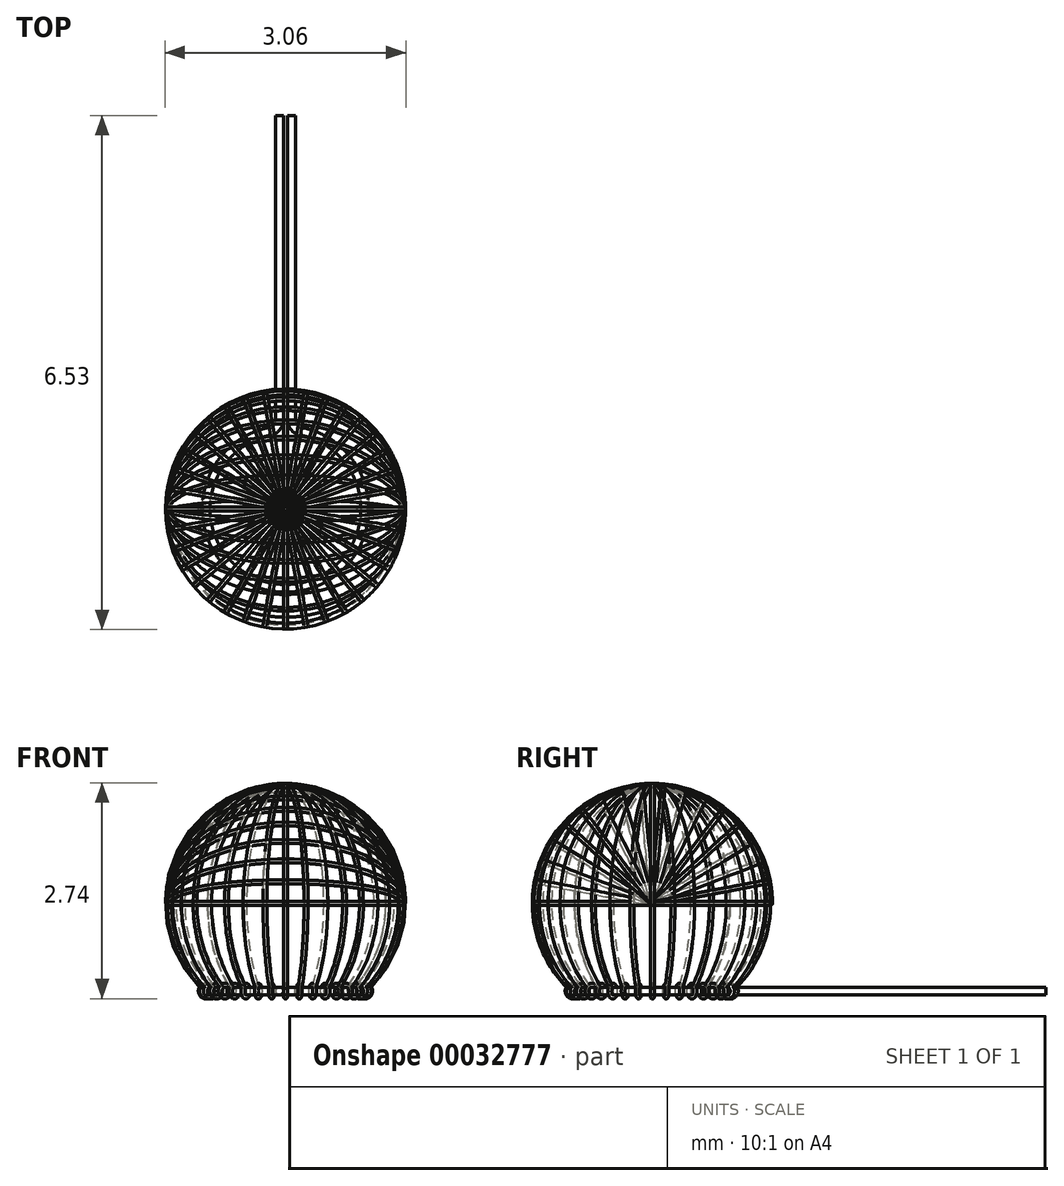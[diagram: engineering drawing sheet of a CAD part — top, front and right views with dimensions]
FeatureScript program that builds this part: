
annotation { "Feature Type Name" : "Feature", "Feature Type Description" : "" }
export const myFeature = defineFeature(function(context is Context, id is Id, definition is map)
    precondition{}
    {
        {
            var Q0;
            Q0=qCreatedBy(makeId("Right.planeOp"),FACE);
            var sketch = newSketch(context, id + "F0", { "sketchPlane" : qUnion([Q0])});
            skArc(sketch, "E0", {"start": v(1.06, -1.06) * mm, "mid": v(0, 1.5) * mm, "end": v(-1.06, -1.06) * mm});
            skSolve(sketch);
        }
        {
            var Q0;
            Q0=qCreatedBy(makeId("Right.planeOp"),FACE);
            var sketch = newSketch(context, id + "F1", { "sketchPlane" : qUnion([Q0])});
            skLineSegment(sketch, "E1", {"start": v(0, 2.55) * mm, "end": v(0, -1.6) * mm});
            skSolve(sketch);
        }
        {
            var Q0;
            Q0=qCreatedBy(makeId("Top.planeOp"),FACE);
            var sketch = newSketch(context, id + "F2", { "sketchPlane" : qUnion([Q0])});
            skArc(sketch, "E2", {"start": v(-1.5, 0) * mm, "mid": v(0, -1.5) * mm, "end": v(1.5, 0) * mm});
            skSolve(sketch);
        }
        {
            var Q0;
            Q0=qCreatedBy(makeId("Front.planeOp"),FACE);
            var sketch = newSketch(context, id + "F3", { "sketchPlane" : qUnion([Q0])});
            skCircle(sketch, "E3", {"center": v(1.5, 0) * mm, "radius": 0.03 * mm});
            skSolve(sketch);
        }
        {
            var Q0;
            Q0 = qSketchRegion(id + "F3", true);
            var Q1;
            Q1=sQuery(id+"F2.wireOp",EDGE,"E2");
            sweep(context, id + "F4", {"profiles" : qUnion([Q0]), "path" : qUnion([Q1])});
        }
        {
            var Q0;
            Q0=qCreatedBy(makeId("Top.planeOp"),FACE);
            var sketch = newSketch(context, id + "F5", { "sketchPlane" : qUnion([Q0])});
            skLineSegment(sketch, "E4", {"start": v(-2.16, 0) * mm, "end": v(2.32, 0) * mm});
            skSolve(sketch);
        }
        {
            var Q0;
            Q0=makeQuery(id+"F4.opSweep","SWEPT_BODY",BODY,{"disambiguationData":[OSD([sQuery(id+"F2.wireOp",EDGE,"E2"),sQuery(id+"F3.wireOp",EDGE,"E3")])]});
            var Q1;
            Q1=sQuery(id+"F5.wireOp",EDGE,"E4");
            circularPattern(context, id + "F6", {"entities" : qUnion([Q0]), "axis" : qUnion([Q1]), "angle" : 180 * degree, "instanceCount" : 18, "oppositeDirection" : true, "equalSpace" : true});
        }
        {
            var Q0;
            Q0=qCreatedBy(makeId("Right.planeOp"),FACE);
            cPlane(context, id + "F7", {"entities" : qUnion([Q0]), "cplaneType" : CPlaneType.OFFSET, "offset" : .5 * mm, "width" : 150 * mm, "height" : 150 * mm});
        }
        {
            var Q0;
            Q0=qCreatedBy(id+"F7.planeOp",FACE);
            var sketch = newSketch(context, id + "F8", { "sketchPlane" : qUnion([Q0])});
            skLineSegment(sketch, "E5", {"start": v(0, 0) * mm, "end": v(-1.06, -1.06) * mm});
            skSolve(sketch);
        }
        {
            var Q0;
            Q0=sQuery(id+"F8.wireOp",EDGE,"E5");
            cPlane(context, id + "F9", {"entities" : qUnion([Q0]), "cplaneType" : CPlaneType.LINE_ANGLE, "offset" : 0 * mm, "angle" : 0 * degree, "width" : 150 * mm, "height" : 150 * mm});
        }
        {
            var Q0;
            Q0=qCreatedBy(id+"F9.planeOp",FACE);
            var sketch = newSketch(context, id + "F10", { "sketchPlane" : qUnion([Q0])});
            skCircle(sketch, "E6", {"center": v(0, -1.5) * mm, "radius": 0.03 * mm});
            skSolve(sketch);
        }
        {
            var Q0;
            Q0=makeQuery(id+"F10.imprint","IMPRINT",FACE,{"disambiguationData":[TD([[makeQuery(id+"F10.imprint","IMPRINT",EDGE,{"derivedFrom":sQuery(id+"F10.wireOp",EDGE,"E6")}),1.0]])]});
            var Q1;
            Q1=sQuery(id+"F0.wireOp",EDGE,"E0");
            sweep(context, id + "F11", {"profiles" : qUnion([Q0]), "path" : qUnion([Q1])});
        }
        {
            var Q0;
            Q0=makeQuery(id+"F11.opSweep","SWEPT_BODY",BODY,{"disambiguationData":[OSD([sQuery(id+"F0.wireOp",EDGE,"E0"),sQuery(id+"F10.wireOp",EDGE,"E6")])]});
            var Q1;
            Q1=sQuery(id+"F1.wireOp",EDGE,"E1");
            circularPattern(context, id + "F12", {"entities" : qUnion([Q0]), "axis" : qUnion([Q1]), "angle" : 360 * degree, "instanceCount" : 36, "equalSpace" : true});
        }
        {
            var Q0;
            Q0=qCreatedBy(makeId("Right.planeOp"),FACE);
            var sketch = newSketch(context, id + "F13", { "sketchPlane" : qUnion([Q0])});
            skLineSegment(sketch, "E7", {"start": v(0, 0) * mm, "end": v(-1.06, -1.06) * mm});
            skCircle(sketch, "E8", {"center": v(-1, -1.11) * mm, "radius": 0.07 * mm});
            skCircle(sketch, "E9", {"center": v(1, -1.11) * mm, "radius": 0.02 * mm});
            skSolve(sketch);
        }
        {
            var Q0;
            Q0=sQuery(id+"F13.wireOp",VERTEX,"E7.end");
            var Q1;
            Q1=sQuery(id+"F13.wireOp",EDGE,"E8");
            cPlane(context, id + "F14", {"entities" : qUnion([Q0, Q1]), "cplaneType" : CPlaneType.CURVE_POINT, "offset" : 150 * mm, "width" : 150 * mm, "height" : 150 * mm});
        }
        {
            var Q0;
            Q0=qCreatedBy(id+"F14.planeOp",FACE);
            var sketch = newSketch(context, id + "F15", { "sketchPlane" : qUnion([Q0])});
            skCircle(sketch, "E10", {"center": v(0, 0) * mm, "radius": 0.03 * mm});
            skSolve(sketch);
        }
        {
            var Q0;
            Q0=makeQuery(id+"F15.imprint","IMPRINT",FACE,{"disambiguationData":[TD([[makeQuery(id+"F15.imprint","IMPRINT",EDGE,{"derivedFrom":sQuery(id+"F15.wireOp",EDGE,"E10")}),1.0]])]});
            var Q1;
            Q1=sQuery(id+"F13.wireOp",EDGE,"E8");
            sweep(context, id + "F16", {"profiles" : qUnion([Q0]), "path" : qUnion([Q1])});
        }
        {
            var Q0;
            Q0=qCreatedBy(id+"F9.planeOp",FACE);
            var sketch = newSketch(context, id + "F17", { "sketchPlane" : qUnion([Q0])});
            skLineSegment(sketch, "E11", {"start": v(0, 3.07) * mm, "end": v(0, -3.64) * mm});
            skSolve(sketch);
        }
        {
            var Q0;
            Q0=qCreatedBy(makeId("Front.planeOp"),FACE);
            var sketch = newSketch(context, id + "F18", { "sketchPlane" : qUnion([Q0])});
            skLineSegment(sketch, "E12", {"start": v(0, -1.63) * mm, "end": v(0, 2.34) * mm});
            skSolve(sketch);
        }
        {
            var Q0;
            Q0=makeQuery(id+"F16.opSweep","SWEPT_BODY",BODY,{"disambiguationData":[OSD([sQuery(id+"F13.wireOp",EDGE,"E8"),sQuery(id+"F15.wireOp",EDGE,"E10")])]});
            var Q1;
            Q1=sQuery(id+"F18.wireOp",EDGE,"E12");
            circularPattern(context, id + "F19", {"entities" : qUnion([Q0]), "axis" : qUnion([Q1]), "angle" : 360 * degree, "instanceCount" : 36, "equalSpace" : true});
        }
        {
            var Q0;
            Q0=qCreatedBy(makeId("Top.planeOp"),FACE);
            var Q1;
            Q1=sQuery(id+"F13.wireOp",VERTEX,"E9.center");
            cPlane(context, id + "F20", {"entities" : qUnion([Q0, Q1]), "cplaneType" : CPlaneType.PLANE_POINT, "offset" : 150 * mm, "width" : 150 * mm, "height" : 150 * mm});
        }
        {
            var Q0;
            Q0=qCreatedBy(id+"F20.planeOp",FACE);
            var sketch = newSketch(context, id + "F21", { "sketchPlane" : qUnion([Q0])});
            skArc(sketch, "E13", {"start": v(-0.2, 0.99) * mm, "mid": v(0, -1) * mm, "end": v(0.2, 0.99) * mm});
            skLineSegment(sketch, "E14", {"start": v(-0.07, 1.14) * mm, "end": v(-0.07, 5) * mm});
            skLineSegment(sketch, "E15", {"start": v(0.07, 1.14) * mm, "end": v(0.07, 5) * mm});
            skPoint(sketch, "E16.visualSharp", {"position": v(-0.07, 1) * mm});
            skArc(sketch, "E16.filletArc", {"start": v(-0.2, 0.99) * mm, "mid": v(-0.1, 1.04) * mm, "end": v(-0.07, 1.14) * mm});
            skPoint(sketch, "E17.visualSharp", {"position": v(0.07, 1) * mm});
            skArc(sketch, "E17.filletArc", {"start": v(0.07, 1.14) * mm, "mid": v(0.1, 1.04) * mm, "end": v(0.2, 0.99) * mm});
            skSolve(sketch);
        }
        {
            var Q0;
            Q0=qCreatedBy(makeId("Front.planeOp"),FACE);
            cPlane(context, id + "F22", {"entities" : qUnion([Q0]), "cplaneType" : CPlaneType.OFFSET, "offset" : 5 * mm, "oppositeDirection" : true, "width" : 150 * mm, "height" : 150 * mm});
        }
        {
            var Q0;
            Q0=qCreatedBy(id+"F22.planeOp",FACE);
            var sketch = newSketch(context, id + "F23", { "sketchPlane" : qUnion([Q0])});
            skCircle(sketch, "E18", {"center": v(-0.07, -1.11) * mm, "radius": 0.05 * mm});
            skSolve(sketch);
        }
        {
            var Q0;
            Q0=qCreatedBy(makeId("Front.planeOp"),FACE);
            cPlane(context, id + "F24", {"entities" : qUnion([Q0]), "cplaneType" : CPlaneType.OFFSET, "offset" : 1.5 * mm, "oppositeDirection" : true, "width" : 150 * mm, "height" : 150 * mm});
        }
        {
            var Q0;
            Q0=qCreatedBy(id+"F24.planeOp",FACE);
            var sketch = newSketch(context, id + "F25", { "sketchPlane" : qUnion([Q0])});
            skLineSegment(sketch, "E19.bottom", {"start": v(0.02, -0.03) * mm, "end": v(-0.03, -0.03) * mm});
            skLineSegment(sketch, "E19.top", {"start": v(0.03, -1.25) * mm, "end": v(-0.02, -1.25) * mm});
            skLineSegment(sketch, "E19.left", {"start": v(0.02, -0.02) * mm, "end": v(0.02, -1.25) * mm});
            skLineSegment(sketch, "E19.right", {"start": v(-0.03, -0.02) * mm, "end": v(-0.03, -1.25) * mm});
            skSolve(sketch);
        }
        {
            var Q0;
            Q0=makeQuery(id+"F25.imprint","IMPRINT",FACE,{"disambiguationData":[TD([[makeQuery(id+"F25.imprint","IMPRINT",EDGE,{"derivedFrom":sQuery(id+"F25.wireOp",EDGE,"E19.bottom")}),1.0]])]});
            var Q1;
            Q1=sQuery(id+"F25.wireOp",EDGE,"E19.right");
            extrude(context, id + "F26", {"entities" : qUnion([Q0]), "operationType" : NewBodyOperationType.REMOVE, "surfaceEntities" : qUnion([Q1]), "endBound" : BoundingType.SYMMETRIC, "depth" : 2 * mm});
        }
        {
            var Q0;
            Q0=makeQuery(id+"F23.imprint","IMPRINT",FACE,{"disambiguationData":[TD([[makeQuery(id+"F23.imprint","IMPRINT",EDGE,{"derivedFrom":sQuery(id+"F23.wireOp",EDGE,"E18")}),1.0]])]});
            var Q1;
            Q1=sQuery(id+"F21.wireOp",EDGE,"E14");
            var Q2;
            Q2=sQuery(id+"F21.wireOp",EDGE,"E16.filletArc");
            var Q3;
            Q3=sQuery(id+"F21.wireOp",EDGE,"E13");
            var Q4;
            Q4=sQuery(id+"F21.wireOp",EDGE,"E17.filletArc");
            var Q5;
            Q5=sQuery(id+"F21.wireOp",EDGE,"E15");
            sweep(context, id + "F27", {"profiles" : qUnion([Q0]), "path" : qUnion([Q1, Q2, Q3, Q4, Q5])});
        }
        {
            var Q0;
            Q0=qCreatedBy(makeId("Right.planeOp"),FACE);
            var sketch = newSketch(context, id + "F28", { "sketchPlane" : qUnion([Q0])});
            skArc(sketch, "E20", {"start": v(1.47, 0) * mm, "mid": v(1.5, -0.02) * mm, "end": v(1.53, 0) * mm});
            skLineSegment(sketch, "E21", {"start": v(1.52, -0.02) * mm, "end": v(1.47, -0.03) * mm});
            skArc(sketch, "E22", {"start": v(1.52, -0.03) * mm, "mid": v(1.52, -0.01) * mm, "end": v(1.52, 0) * mm});
            skArc(sketch, "E23", {"start": v(1.47, -0.03) * mm, "mid": v(1.47, -0.01) * mm, "end": v(1.47, 0) * mm});
            skSolve(sketch);
        }
        {
            var Q0;
            Q0=qCreatedBy(makeId("Right.planeOp"),FACE);
            var sketch = newSketch(context, id + "F29", { "sketchPlane" : qUnion([Q0])});
            skLineSegment(sketch, "E24", {"start": v(0, 1.76) * mm, "end": v(0, -1.5) * mm});
            skSolve(sketch);
        }
        {
            var Q0;
            Q0 = qSketchRegion(id + "F28", true);
            var Q1;
            Q1 = qConstructionFilter(qBodyType(qCreatedBy(id + "F28" ,EDGE), BodyType.WIRE), ConstructionObject.NO);
            var Q2;
            Q2=sQuery(id+"F29.wireOp",EDGE,"E24");
            revolve(context, id + "F30", {"operationType" : NewBodyOperationType.REMOVE, "entities" : qUnion([Q0]), "surfaceEntities" : qUnion([Q1]), "axis" : qUnion([Q2]), "revolveType" : RevolveType.SYMMETRIC, "oppositeDirection" : true, "angle" : 2.06 * degree});
        }
    });
